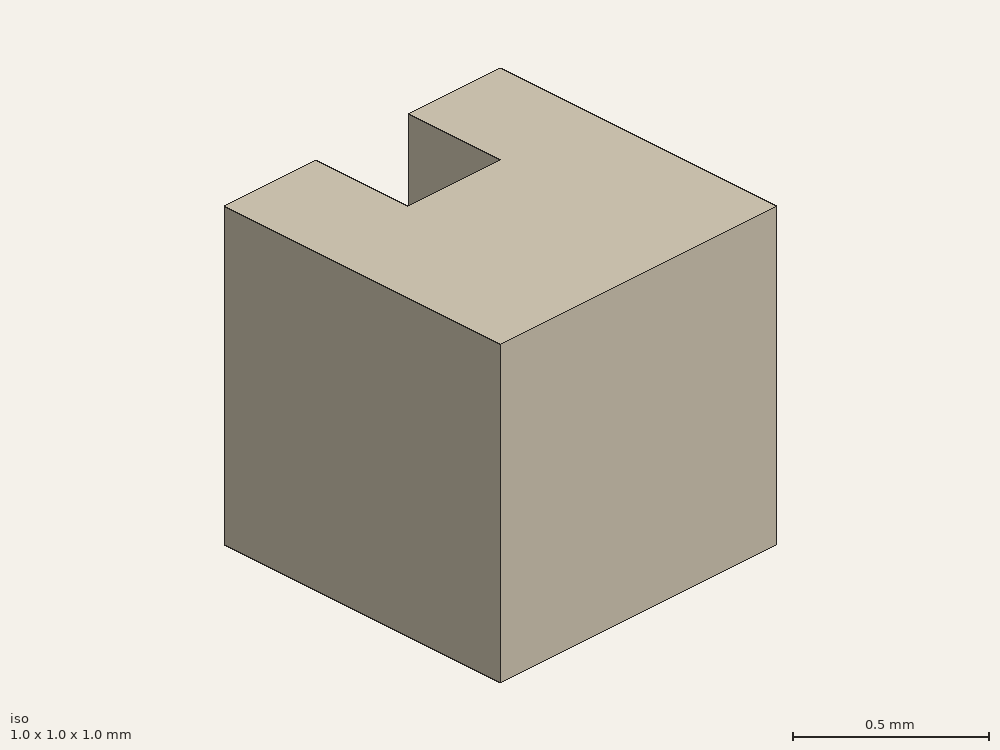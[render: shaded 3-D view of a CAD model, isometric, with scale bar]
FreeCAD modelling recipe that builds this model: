
FCSTD DOCUMENT  (FreeCAD 1.0R38642 (Git))
Label: cube_1x1x1_PointOnObject
License: All rights reserved
LicenseURL: http://en.wikipedia.org/wiki/All_rights_reserved
objects: Sketcher::SketchObject×1, PartDesign::Pad×1, PartDesign::Body×1
note: 6 computed .brp shape members not serialized (recipe doc carries the construction recipe); baked Part::Feature solids carry a one-line shape summary decoded from their .brp

FEATURE [Sketcher::SketchObject] Sketch
  ArcFitTolerance = 1e-06
  AttachmentSupport = -> [XY_Plane]
  FullyConstrained = true
  MakeInternals = false
  MapMode = 5
  sketch-geometry (8):
    g0: LineSegment StartX=0 StartY=1 StartZ=0 EndX=0.333333 EndY=1 EndZ=0
    g1: LineSegment StartX=1 StartY=1 StartZ=0 EndX=1 EndY=0 EndZ=0
    g2: LineSegment StartX=0 StartY=1 StartZ=0 EndX=0 EndY=0 EndZ=0
    g3: LineSegment StartX=1 StartY=0 StartZ=0 EndX=0 EndY=0 EndZ=0
    g4: LineSegment StartX=0.333333 StartY=1 StartZ=0 EndX=0.333333 EndY=0.666667 EndZ=0
    g5: LineSegment StartX=0.333333 StartY=0.666667 StartZ=0 EndX=0.666667 EndY=0.666667 EndZ=0
    g6: LineSegment StartX=0.666667 StartY=0.666667 StartZ=0 EndX=0.666667 EndY=1 EndZ=0
    g7: LineSegment StartX=0.666667 StartY=1 StartZ=0 EndX=1 EndY=1 EndZ=0
  constraints (23):
    c: Horizontal(g0)
    c: Vertical(g1)
    c: Coincident(g2,g0)
    c: Vertical(g2)
    c: Coincident(g3,g1)
    c: Coincident(g3,g2)
    c: Horizontal(g3)
    c: Equal(g2,g3)
    c: DistanceY(g2,g2) = 1
    c: PointOnObject(g-1,g2)
    c: PointOnObject(g-1,g3)
    c: Coincident(g4,g0)
    c: Vertical(g4)
    c: Coincident(g5,g4)
    c: Horizontal(g5)
    c: Coincident(g6,g5)
    c: Vertical(g6)
    c: Coincident(g7,g1)
    c: Tangent(g0,g7)
    c: Coincident(g6,g7)
    c: Equal(g0,g4)
    c: Equal(g0,g7)
    c: Equal(g0,g5)
FEATURE [PartDesign::Pad] Pad
  Direction = (0,0,1)
  Length = 1
  Length2 = 10
  Profile = -> Sketch
  ReferenceAxis = -> Sketch [N_Axis]
  Refine = true
  Suppressed = false
  Type = 0
FEATURE [PartDesign::Body] Body
  AllowCompound = false
  Group = -> [Sketch,Pad]
  Origin = -> Origin
  Tip = -> Pad
